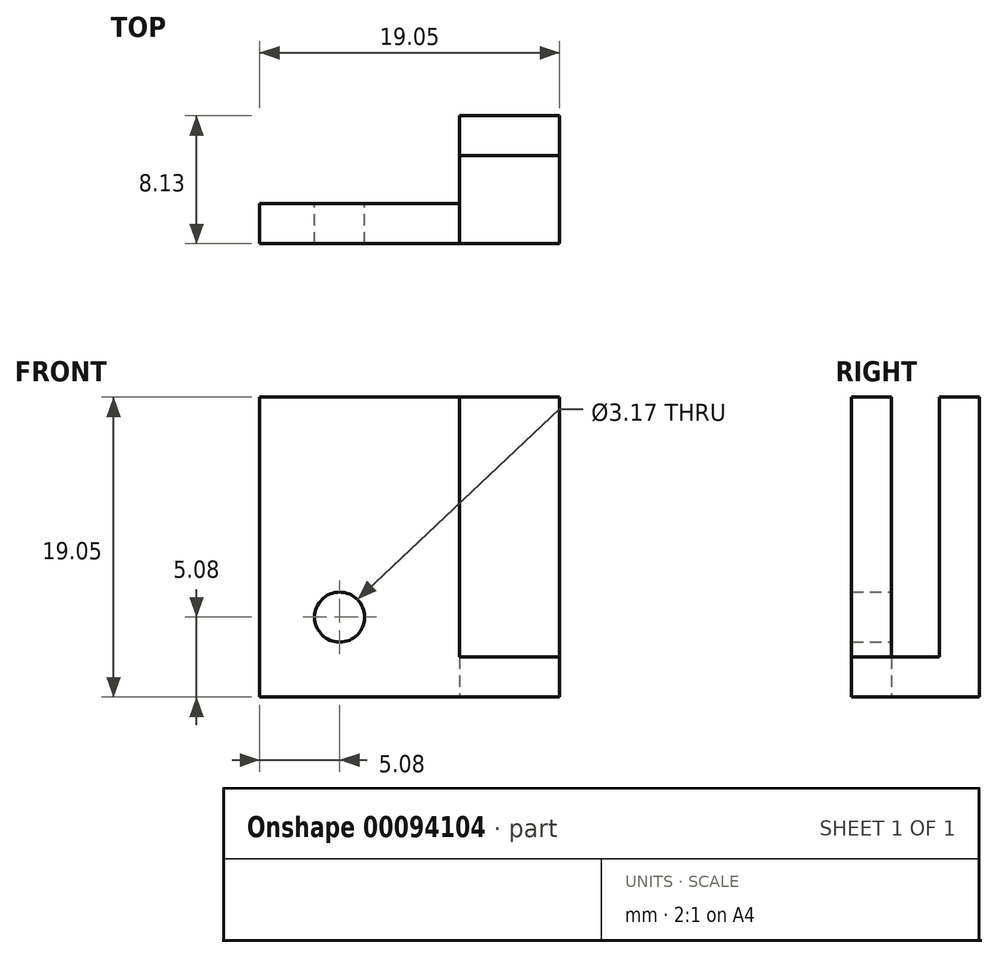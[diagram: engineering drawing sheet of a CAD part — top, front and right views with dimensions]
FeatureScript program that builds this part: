
annotation { "Feature Type Name" : "Feature", "Feature Type Description" : "" }
export const myFeature = defineFeature(function(context is Context, id is Id, definition is map)
    precondition{}
    {
        {
            var Q0;
            Q0=qCreatedBy(makeId("Top.planeOp"),FACE);
            var sketch = newSketch(context, id + "F0", { "sketchPlane" : qUnion([Q0])});
            skLineSegment(sketch, "E0.bottom", {"start": v(0, 0) * mm, "end": v(12.7, 0) * mm});
            skLineSegment(sketch, "E0.top", {"start": v(0, 2.54) * mm, "end": v(12.7, 2.54) * mm});
            skLineSegment(sketch, "E0.left", {"start": v(0, 0) * mm, "end": v(0, 2.54) * mm});
            skLineSegment(sketch, "E0.right", {"start": v(12.7, 0) * mm, "end": v(12.7, 2.54) * mm});
            skLineSegment(sketch, "E1.bottom", {"start": v(12.7, 2.54) * mm, "end": v(10.16, 2.54) * mm});
            skLineSegment(sketch, "E1.top", {"start": v(12.7, 8.13) * mm, "end": v(10.16, 8.13) * mm});
            skLineSegment(sketch, "E1.left", {"start": v(12.7, 2.54) * mm, "end": v(12.7, 8.13) * mm});
            skLineSegment(sketch, "E1.right", {"start": v(10.16, 2.54) * mm, "end": v(10.16, 8.13) * mm});
            skLineSegment(sketch, "E2.bottom", {"start": v(12.7, 8.13) * mm, "end": v(19.05, 8.13) * mm});
            skLineSegment(sketch, "E2.top", {"start": v(12.7, 5.59) * mm, "end": v(19.05, 5.59) * mm});
            skLineSegment(sketch, "E2.left", {"start": v(12.7, 8.13) * mm, "end": v(12.7, 5.59) * mm});
            skLineSegment(sketch, "E2.right", {"start": v(19.05, 8.13) * mm, "end": v(19.05, 5.59) * mm});
            skSolve(sketch);
        }
        {
            var Q0;
            Q0=makeQuery(id+"F0.imprint","IMPRINT",FACE,{"disambiguationData":[TD([[makeQuery(id+"F0.imprint","IMPRINT",EDGE,{"derivedFrom":sQuery(id+"F0.wireOp",EDGE,"E2.bottom")}),-1.0]])]});
            var Q1;
            Q1=makeQuery(id+"F0.imprint","IMPRINT",FACE,{"disambiguationData":[TD([[makeQuery(id+"F0.imprint","IMPRINT",EDGE,{"derivedFrom":sQuery(id+"F0.wireOp",EDGE,"E1.bottom")}),-1.0]])]});
            var Q2;
            Q2=makeQuery(id+"F0.imprint","IMPRINT",FACE,{"disambiguationData":[TD([[makeQuery(id+"F0.imprint","IMPRINT",EDGE,{"derivedFrom":sQuery(id+"F0.wireOp",EDGE,"E0.bottom")}),1.0]])]});
            extrude(context, id + "F1", {"entities" : qUnion([Q0, Q1, Q2]), "depth" : 19.05 * mm});
        }
        {
            var Q0;
            Q0=makeQuery(id+"F1.opExtrude","CAP_FACE",FACE,{"disambiguationData":[OSD([sQuery(id+"F0.wireOp",EDGE,"E0.bottom"),sQuery(id+"F0.wireOp",EDGE,"E0.top"),sQuery(id+"F0.wireOp",EDGE,"E0.left"),sQuery(id+"F0.wireOp",EDGE,"E0.right"),sQuery(id+"F0.wireOp",EDGE,"E1.top"),sQuery(id+"F0.wireOp",EDGE,"E1.left"),sQuery(id+"F0.wireOp",EDGE,"E1.right"),sQuery(id+"F0.wireOp",EDGE,"E2.bottom"),sQuery(id+"F0.wireOp",EDGE,"E2.top"),sQuery(id+"F0.wireOp",EDGE,"E2.right")])],"isStart":true});
            var sketch = newSketch(context, id + "F2", { "sketchPlane" : qUnion([Q0])});
            skLineSegment(sketch, "E3.0", {"start": v(12.7, 0) * mm, "end": v(12.7, -5.59) * mm});
            skLineSegment(sketch, "E4.0", {"start": v(12.7, -5.59) * mm, "end": v(19.05, -5.59) * mm});
            skLineSegment(sketch, "E5.bottom", {"start": v(12.7, 0) * mm, "end": v(19.05, 0) * mm});
            skLineSegment(sketch, "E5.right", {"start": v(19.05, 0) * mm, "end": v(19.05, -5.59) * mm});
            skSolve(sketch);
        }
        {
            var Q0;
            Q0=makeQuery(id+"F2.imprint","IMPRINT",FACE,{"disambiguationData":[TD([[makeQuery(id+"F2.imprint","IMPRINT",EDGE,{"derivedFrom":sQuery(id+"F2.wireOp",EDGE,"E5.bottom")}),-1.0]])]});
            extrude(context, id + "F3", {"entities" : qUnion([Q0]), "operationType" : NewBodyOperationType.ADD, "oppositeDirection" : true, "depth" : 2.54 * mm});
        }
        {
            var Q0;
            Q0=makeQuery(id+"F1.opExtrude","SWEPT_FACE",FACE,{"disambiguationData":[OSD([sQuery(id+"F0.wireOp",EDGE,"E0.top")])]});
            var sketch = newSketch(context, id + "F4", { "sketchPlane" : qUnion([Q0])});
            skLineSegment(sketch, "E6", {"start": v(-5.08, 0) * mm, "end": v(-5.08, 19.05) * mm, "construction": true});
            skCircle(sketch, "E7", {"center": v(-5.08, 5.08) * mm, "radius": 1.59 * mm});
            skSolve(sketch);
        }
        {
            var Q0;
            Q0=makeQuery(id+"F4.imprint","IMPRINT",FACE,{"disambiguationData":[TD([[makeQuery(id+"F4.imprint","IMPRINT",EDGE,{"derivedFrom":sQuery(id+"F4.wireOp",EDGE,"E7")}),1.0]])]});
            extrude(context, id + "F5", {"entities" : qUnion([Q0]), "operationType" : NewBodyOperationType.REMOVE, "oppositeDirection" : true, "depth" : 25.4 * mm});
        }
    });
